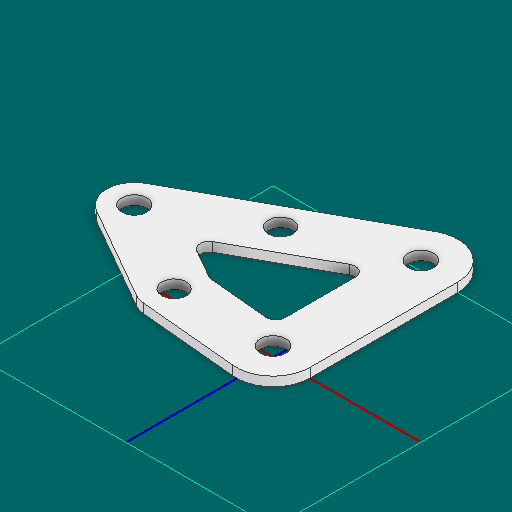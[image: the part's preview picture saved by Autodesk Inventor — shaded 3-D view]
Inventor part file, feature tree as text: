
AUTODESK INVENTOR PART (.ipt)
format: ipt  version: 2025 (Build 290162000, 162)  size: 146,944 bytes
history: native  units: in
note: dims shown in document units (in); Inventor stores cm internally (conversion verified against a paired STEP export)
features: other x3, extrude x1, sketch x1
ambient origin geometry x8: Origin, YZ Plane, XZ Plane, XY Plane, X Axis, Y Axis, Z Axis, Center Point
bodies: Solid1 (feature_tree)
feature tree (5):
  other  "Blocks"
  extrude  "Extrusion1"  Depth=0.375in
  sketch  "Sketch1"  dims[d0=0.165in d1=0.5in d2=0.5in d3=0.375in d4=0.375in d5=0.0625in d6=0.0625in d7=0.0in d8=0.1875in d9=0.165in]
  other  "main"
  other  "main:1"
